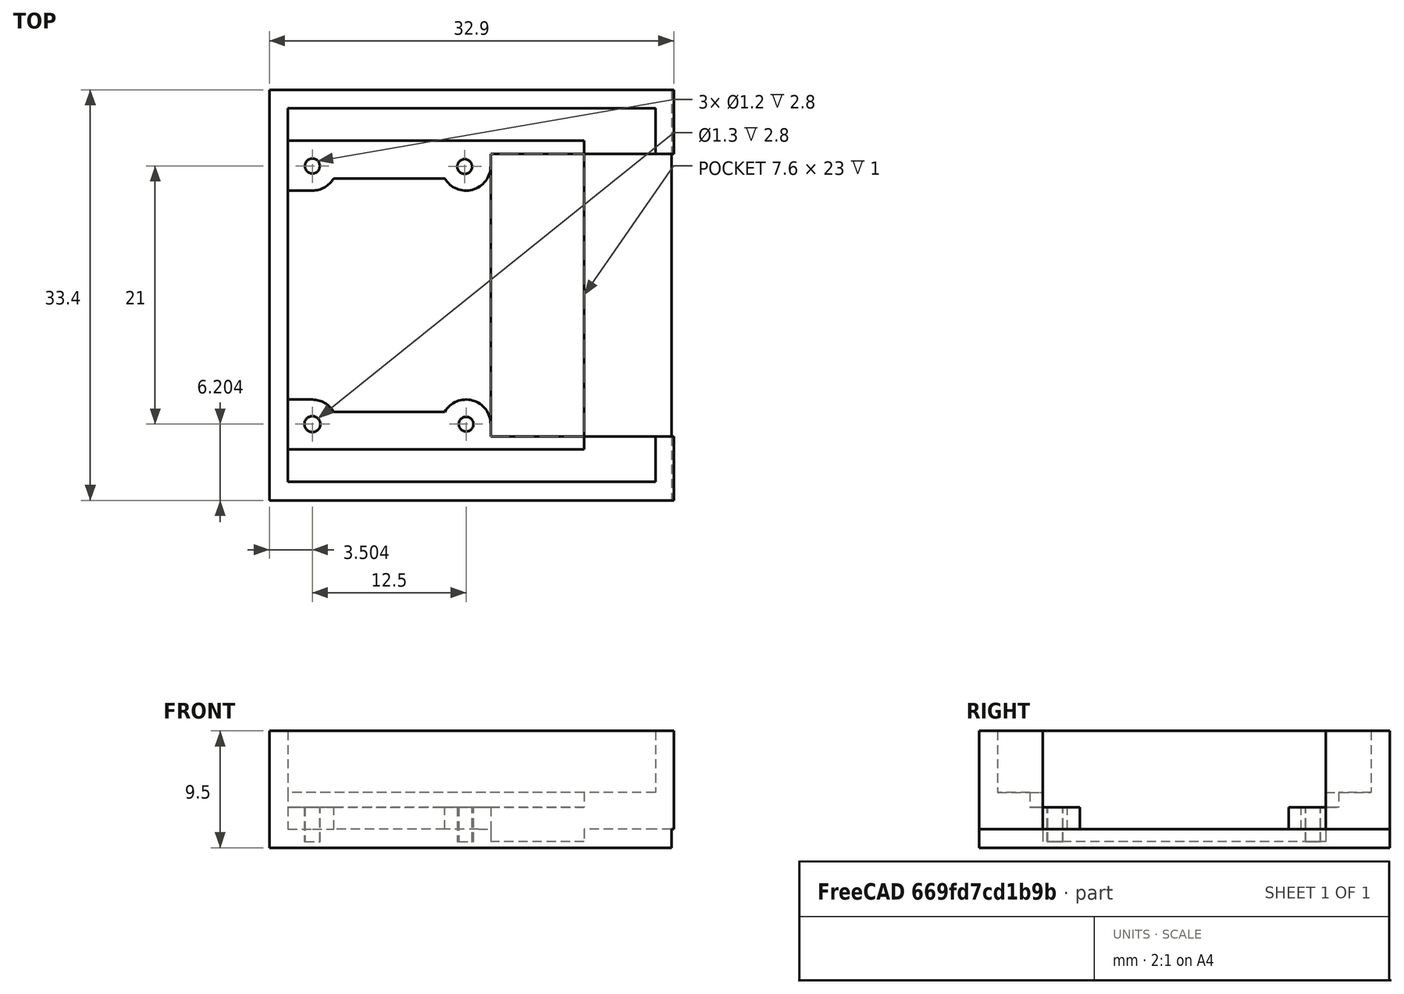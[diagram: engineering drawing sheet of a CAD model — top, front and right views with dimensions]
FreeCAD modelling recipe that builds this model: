
FCSTD DOCUMENT  (FreeCAD 0.18.3R)
Label: Lens.Capsule
License: All rights reserved
LicenseURL: http://en.wikipedia.org/wiki/All_rights_reserved
objects: Part::Part2DObjectPython×21, Part::Extrusion×21, Part::Cut×11, Part::MultiFuse×6
note: 59 computed .brp shape members not serialized (recipe doc carries the construction recipe); baked Part::Feature solids carry a one-line shape summary decoded from their .brp

FEATURE [Part::Part2DObjectPython] Circle018  # Draft 2D object (typed FeaturePython)
  FirstAngle = 0
  LastAngle = 0
  MakeFace = true
  Placement = pos=(80.1343,-53.566,-3.6) rot=(0,0,1;0rad)
  Radius = 2
FEATURE [Part::Part2DObjectPython] Circle019  # Draft 2D object (typed FeaturePython)
  FirstAngle = 0
  LastAngle = 0
  MakeFace = true
  Placement = pos=(80.1343,-74.566,-3.6) rot=(0,0,1;0rad)
  Radius = 2
FEATURE [Part::Part2DObjectPython] Circle020  # Draft 2D object (typed FeaturePython)
  FirstAngle = 0
  LastAngle = 0
  MakeFace = true
  Placement = pos=(67.6343,-74.566,-3.6) rot=(0,0,1;0rad)
  Radius = 2
FEATURE [Part::Part2DObjectPython] Circle021  # Draft 2D object (typed FeaturePython)
  FirstAngle = 0
  LastAngle = 0
  MakeFace = true
  Placement = pos=(67.6343,-53.566,-3.6) rot=(0,0,1;0rad)
  Radius = 2
FEATURE [Part::Part2DObjectPython] Rectangle060  # Draft 2D object (typed FeaturePython)
  ChamferSize = 0
  Columns = 1
  FilletRadius = 0
  Height = 23
  Length = 14.4
  MakeFace = true
  Placement = pos=(52.2343,-52.566,-9.8) rot=(1,0,0;3.14159rad)
  Rows = 1
FEATURE [Part::Part2DObjectPython] Rectangle053  # Draft 2D object (typed FeaturePython)
  ChamferSize = 0
  Columns = 1
  FilletRadius = 0
  Height = 33.4
  Length = 32.9
  MakeFace = true
  Placement = pos=(50.7343,-47.366,-9.8) rot=(1,0,0;3.14159rad)
  Rows = 1
FEATURE [Part::Part2DObjectPython] Rectangle061  # Draft 2D object (typed FeaturePython)
  ChamferSize = 0
  Columns = 1
  FilletRadius = 0
  Height = 25.1
  Length = 24.1
  MakeFace = true
  Placement = pos=(58.0343,-51.516,-9.8) rot=(1,0,0;3.14159rad)
  Rows = 1
FEATURE [Part::Part2DObjectPython] Rectangle059  # Draft 2D object (typed FeaturePython)
  ChamferSize = 0
  Columns = 1
  FilletRadius = 0
  Height = 19
  Length = 15.5
  MakeFace = true
  Placement = pos=(66.6343,-54.566,-9.8) rot=(1,0,0;3.14159rad)
  Rows = 1
FEATURE [Part::Part2DObjectPython] Rectangle062  # Draft 2D object (typed FeaturePython)
  ChamferSize = 0
  Columns = 1
  FilletRadius = 0
  Height = 30.4
  Length = 29.9
  MakeFace = true
  Placement = pos=(52.2343,-48.866,-9.8) rot=(1,0,0;3.14159rad)
  Rows = 1
FEATURE [Part::Extrusion] Extrude107
  Base = -> Rectangle053
  Dir = (0,0,-1)
  DirMode = 2
  FaceMakerClass = Part::FaceMakerBullseye
  LengthFwd = -9
  LengthRev = 0
  Solid = false
  Symmetric = false
FEATURE [Part::Extrusion] Extrude116
  Base = -> Rectangle062
  Dir = (0,0,-1)
  DirMode = 2
  FaceMakerClass = Part::FaceMakerBullseye
  LengthFwd = -5
  LengthRev = 0
  Solid = false
  Symmetric = false
FEATURE [Part::Cut] Cut046
  Base = -> Extrude107
  Tool = -> Extrude116
FEATURE [Part::Extrusion] Extrude117
  Base = -> Rectangle061
  Dir = (0,0,-1)
  DirMode = 2
  FaceMakerClass = Part::FaceMakerBullseye
  LengthFwd = -6.2
  LengthRev = 0
  Solid = false
  Symmetric = false
FEATURE [Part::Part2DObjectPython] Rectangle063  # Draft 2D object (typed FeaturePython)
  ChamferSize = 0
  Columns = 1
  FilletRadius = 0
  Height = 23
  Length = 1.5
  MakeFace = true
  Placement = pos=(50.7343,-75.566,-9.8) rot=(0,0,1;0rad)
  Rows = 1
FEATURE [Part::Extrusion] Extrude128
  Base = -> Rectangle063
  Dir = (0,0,1)
  DirMode = 2
  FaceMakerClass = Part::FaceMakerBullseye
  LengthFwd = 8
  LengthRev = 0
  Solid = false
  Symmetric = false
FEATURE [Part::Part2DObjectPython] Rectangle064  # Draft 2D object (typed FeaturePython)
  ChamferSize = 0
  Columns = 1
  FilletRadius = 0
  Height = 1
  Length = 2
  MakeFace = true
  Placement = pos=(80.1343,-73.566,-3.6) rot=(0,0,1;0rad)
  Rows = 1
FEATURE [Part::Part2DObjectPython] Rectangle065  # Draft 2D object (typed FeaturePython)
  ChamferSize = 0
  Columns = 1
  FilletRadius = 0
  Height = 1
  Length = 2
  MakeFace = true
  Placement = pos=(80.1343,-55.566,-3.6) rot=(0,0,1;0rad)
  Rows = 1
FEATURE [Part::Part2DObjectPython] Rectangle066  # Draft 2D object (typed FeaturePython)
  ChamferSize = 0
  Columns = 1
  FilletRadius = 0
  Height = 1
  Length = 1
  MakeFace = true
  Placement = pos=(65.6343,-75.566,-3.6) rot=(0,0,1;0rad)
  Rows = 1
FEATURE [Part::Part2DObjectPython] Rectangle067  # Draft 2D object (typed FeaturePython)
  ChamferSize = 0
  Columns = 1
  FilletRadius = 0
  Height = 1
  Length = 1
  MakeFace = true
  Placement = pos=(65.6343,-53.566,-3.6) rot=(0,0,1;0rad)
  Rows = 1
FEATURE [Part::Extrusion] Extrude140
  Base = -> Rectangle059
  Dir = (0,0,-1)
  DirMode = 2
  FaceMakerClass = Part::FaceMakerBullseye
  LengthFwd = -8
  LengthRev = 0
  Solid = false
  Symmetric = false
FEATURE [Part::Extrusion] Extrude141
  Base = -> Rectangle060
  Dir = (0,0,-1)
  DirMode = 2
  FaceMakerClass = Part::FaceMakerBullseye
  LengthFwd = -8
  LengthRev = 0
  Solid = false
  Symmetric = false
FEATURE [Part::Extrusion] Extrude149
  Base = -> Circle020
  Dir = (0,0,1)
  DirMode = 2
  FaceMakerClass = Part::FaceMakerBullseye
  LengthFwd = 2.1
  LengthRev = 0
  Solid = false
  Symmetric = false
FEATURE [Part::Extrusion] Extrude150
  Base = -> Rectangle066
  Dir = (0,0,1)
  DirMode = 2
  FaceMakerClass = Part::FaceMakerBullseye
  LengthFwd = 2.1
  LengthRev = 0
  Solid = false
  Symmetric = false
FEATURE [Part::MultiFuse] Fusion024
  Shapes = -> [Extrude149,Extrude150]
FEATURE [Part::Extrusion] Extrude152
  Base = -> Circle019
  Dir = (0,0,1)
  DirMode = 2
  FaceMakerClass = Part::FaceMakerBullseye
  LengthFwd = 2.1
  LengthRev = 0
  Solid = false
  Symmetric = false
FEATURE [Part::Extrusion] Extrude153
  Base = -> Rectangle064
  Dir = (0,0,1)
  DirMode = 2
  FaceMakerClass = Part::FaceMakerBullseye
  LengthFwd = 2.1
  LengthRev = 0
  Solid = false
  Symmetric = false
FEATURE [Part::Extrusion] Extrude155
  Base = -> Circle018
  Dir = (0,0,1)
  DirMode = 2
  FaceMakerClass = Part::FaceMakerBullseye
  LengthFwd = 2.1
  LengthRev = 0
  Solid = false
  Symmetric = false
FEATURE [Part::Extrusion] Extrude156
  Base = -> Rectangle065
  Dir = (0,0,1)
  DirMode = 2
  FaceMakerClass = Part::FaceMakerBullseye
  LengthFwd = 2.1
  LengthRev = 0
  Solid = false
  Symmetric = false
FEATURE [Part::Extrusion] Extrude158
  Base = -> Circle021
  Dir = (0,0,1)
  DirMode = 2
  FaceMakerClass = Part::FaceMakerBullseye
  LengthFwd = 2.1
  LengthRev = 0
  Solid = false
  Symmetric = false
FEATURE [Part::Extrusion] Extrude159
  Base = -> Rectangle067
  Dir = (0,0,1)
  DirMode = 2
  FaceMakerClass = Part::FaceMakerBullseye
  LengthFwd = 2.1
  LengthRev = 0
  Solid = false
  Symmetric = false
FEATURE [Part::MultiFuse] Fusion025
  Shapes = -> [Extrude158,Extrude159]
FEATURE [Part::Cut] Cut060
  Base = -> Cut046
  Tool = -> Extrude140
FEATURE [Part::Cut] Cut061
  Base = -> Cut060
  Tool = -> Extrude141
FEATURE [Part::Cut] Cut062
  Base = -> Cut061
  Tool = -> Extrude128
FEATURE [Part::Cut] Cut063
  Base = -> Cut062
  Tool = -> Extrude117
FEATURE [Part::Part2DObjectPython] Rectangle070  # Draft 2D object (typed FeaturePython)
  ChamferSize = 0
  Columns = 1
  FilletRadius = 0
  Height = 23
  Length = 7.6
  MakeFace = true
  Placement = pos=(58.0343,-75.566,-3.6) rot=(0,0,1;0rad)
  Rows = 1
FEATURE [Part::Extrusion] Extrude162
  Base = -> Rectangle070
  Dir = (0,0,1)
  DirMode = 2
  FaceMakerClass = Part::FaceMakerBullseye
  LengthFwd = 2.8
  LengthRev = 0
  Solid = false
  Symmetric = false
FEATURE [Part::Cut] Cut074
  Base = -> Cut063
  Tool = -> Extrude162
FEATURE [Part::Part2DObjectPython] Circle036  # Draft 2D object (typed FeaturePython)
  FirstAngle = 0
  LastAngle = 0
  MakeFace = true
  Placement = pos=(80.1343,-53.566,-3.6) rot=(0,0,1;0rad)
  Radius = 0.6
FEATURE [Part::MultiFuse] Fusion026
  Shapes = -> [Extrude156,Extrude155]
FEATURE [Part::Extrusion] Extrude163
  Base = -> Circle036
  Dir = (0,0,1)
  DirMode = 2
  FaceMakerClass = Part::FaceMakerBullseye
  LengthFwd = 2.8
  LengthRev = 0
  Solid = false
  Symmetric = false
FEATURE [Part::Part2DObjectPython] Circle037  # Draft 2D object (typed FeaturePython)
  FirstAngle = 0
  LastAngle = 0
  MakeFace = true
  Placement = pos=(67.7487,-53.6033,-3.6) rot=(1,0,0;3.14159rad)
  Radius = 0.6
FEATURE [Part::Part2DObjectPython] Circle038  # Draft 2D object (typed FeaturePython)
  FirstAngle = 0
  LastAngle = 0
  MakeFace = true
  Placement = pos=(67.6343,-74.566,-3.6) rot=(0,0,1;0rad)
  Radius = 0.6
FEATURE [Part::Extrusion] Extrude165
  Base = -> Circle038
  Dir = (0,0,1)
  DirMode = 2
  FaceMakerClass = Part::FaceMakerBullseye
  LengthFwd = 2.8
  LengthRev = 0
  Solid = false
  Symmetric = false
FEATURE [Part::Extrusion] Extrude166
  Base = -> Circle037
  Dir = (0,0,-1)
  DirMode = 2
  FaceMakerClass = Part::FaceMakerBullseye
  LengthFwd = -2.8
  LengthRev = 0
  Solid = false
  Symmetric = false
FEATURE [Part::Part2DObjectPython] Circle040  # Draft 2D object (typed FeaturePython)
  FirstAngle = 0
  LastAngle = 0
  MakeFace = true
  Placement = pos=(80.1343,-74.566,-3.6) rot=(1,0,0;3.14159rad)
  Radius = 0.65
  Support = -> [Cut074]
FEATURE [Part::Extrusion] Extrude167
  Base = -> Circle040
  Dir = (0,0,-1)
  DirMode = 2
  FaceMakerClass = Part::FaceMakerBullseye
  LengthFwd = -10
  LengthRev = 0
  Solid = false
  Symmetric = false
FEATURE [Part::MultiFuse] Fusion032
  Shapes = -> [Extrude152,Extrude153]
FEATURE [Part::MultiFuse] Fusion033
  Shapes = -> [Fusion025,Fusion026,Fusion032,Fusion024,Cut074]
FEATURE [Part::Cut] Cut075
  Base = -> Fusion033
  Tool = -> Extrude167
FEATURE [Part::Cut] Cut076
  Base = -> Cut075
  Tool = -> Extrude165
FEATURE [Part::Cut] Cut077
  Base = -> Cut076
  Tool = -> Extrude163
FEATURE [Part::Cut] Cut078  label="Cut - Lens Capsule"
  Base = -> Cut077
  Placement = pos=(101.469,0,-19.6) rot=(0,1,0;3.14159rad)
  Tool = -> Extrude166
FEATURE [Part::Part2DObjectPython] Rectangle072  # Draft 2D object (typed FeaturePython)
  ChamferSize = 0
  Columns = 1
  FilletRadius = 0
  Height = 33.4
  Length = 32.9
  MakeFace = true
  Placement = pos=(17.8343,-47.366,-18.8) rot=(1,0,0;3.14159rad)
  Rows = 1
  Support = -> [Cut078]
FEATURE [Part::Extrusion] Extrude172
  Base = -> Rectangle072
  Dir = (1e-16,0,-1)
  DirMode = 2
  FaceMakerClass = Part::FaceMakerBullseye
  LengthFwd = 0.5
  LengthRev = 0
  Solid = false
  Symmetric = false
FEATURE [Part::MultiFuse] Fusion035  label="Fusion - Lens Capsule"
  Shapes = -> [Cut078,Extrude172]
FEATURE [Part::Part2DObjectPython] Rectangle077  # Draft 2D object (typed FeaturePython)
  ChamferSize = 0
  Columns = 1
  FilletRadius = 0
  Height = 33.4
  Length = 0.2
  MakeFace = true
  Placement = pos=(50.5343,-80.766,-19.3) rot=(0,0,1;0rad)
  Rows = 1
FEATURE [Part::Extrusion] Extrude207
  Base = -> Rectangle077
  Dir = (0,0,1)
  DirMode = 2
  FaceMakerClass = Part::FaceMakerBullseye
  LengthFwd = 1.5
  LengthRev = 0
  Solid = false
  Symmetric = false
FEATURE [Part::Cut] Cut108  label="Cut-Lens Capsule"
  Base = -> Fusion035
  Tool = -> Extrude207
